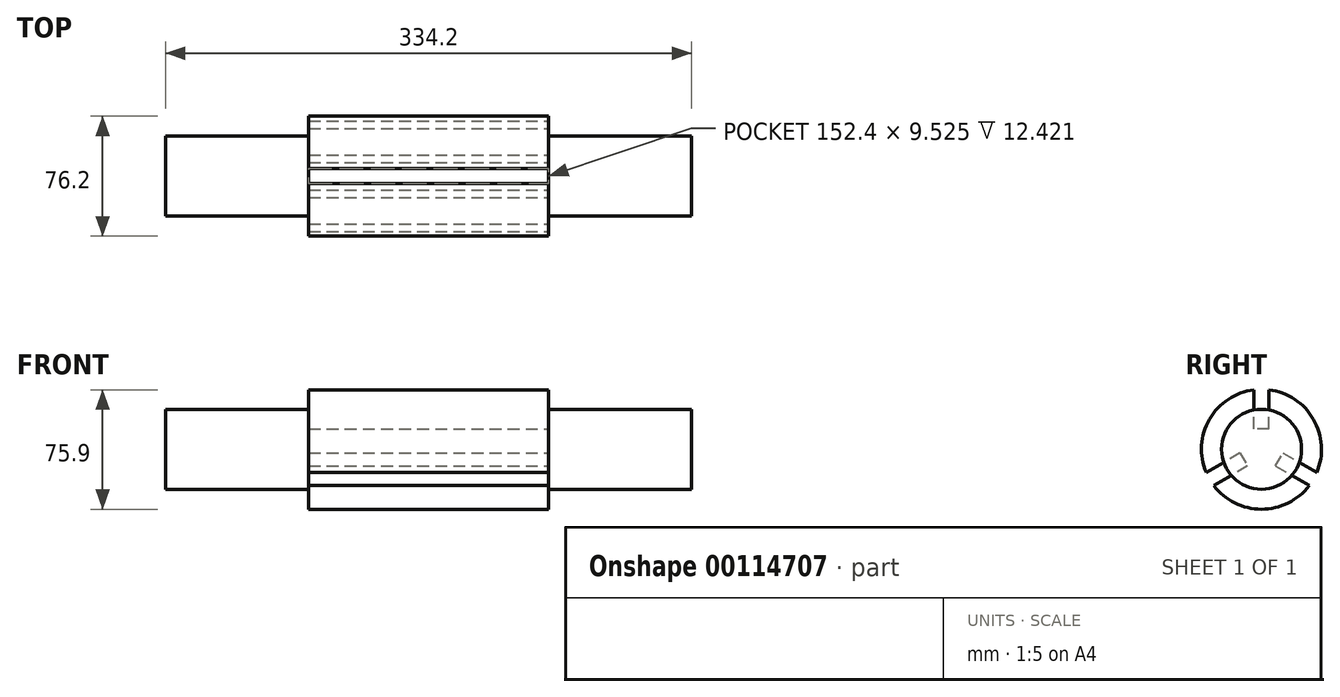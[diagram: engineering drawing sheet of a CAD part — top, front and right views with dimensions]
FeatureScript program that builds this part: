
annotation { "Feature Type Name" : "Feature", "Feature Type Description" : "" }
export const myFeature = defineFeature(function(context is Context, id is Id, definition is map)
    precondition{}
    {
        {
            var Q0;
            Q0=qCreatedBy(makeId("Front.planeOp"),FACE);
            var sketch = newSketch(context, id + "F0", { "sketchPlane" : qUnion([Q0])});
            skLineSegment(sketch, "E0.0", {"start": v(69.85, 0) * mm, "end": v(69.85, 25.4) * mm});
            skLineSegment(sketch, "E1.0", {"start": v(-21.05, 25.4) * mm, "end": v(-21.05, 38.1) * mm});
            skLineSegment(sketch, "E2", {"start": v(69.85, 25.4) * mm, "end": v(-21.05, 25.4) * mm});
            skLineSegment(sketch, "E3.0", {"start": v(-21.05, 38.1) * mm, "end": v(-97.25, 38.1) * mm});
            skLineSegment(sketch, "E4", {"start": v(0, 0) * mm, "end": v(0, 17.35) * mm});
            skLineSegment(sketch, "E5.0", {"start": v(-97.25, 0) * mm, "end": v(-97.25, 38.1) * mm});
            skLineSegment(sketch, "E6.MirrorCS", {"start": v(-173.45, 38.1) * mm, "end": v(-97.25, 38.1) * mm});
            skLineSegment(sketch, "E7.MirrorCS", {"start": v(-173.45, 25.4) * mm, "end": v(-173.45, 38.1) * mm});
            skLineSegment(sketch, "E8.MirrorCS", {"start": v(-264.35, 25.4) * mm, "end": v(-173.45, 25.4) * mm});
            skLineSegment(sketch, "E9.MirrorCS", {"start": v(-264.35, 0) * mm, "end": v(-264.35, 25.4) * mm});
            skLineSegment(sketch, "E10", {"start": v(69.85, 0) * mm, "end": v(-264.35, 0) * mm});
            skSolve(sketch);
        }
        {
            var Q0;
            {var subQ0=sQuery(id+"F0.wireOp",EDGE,"E0.0");Q0=makeQuery(id+"F0.imprint","IMPRINT",FACE,{"disambiguationData":[TD([[makeQuery(id+"F0.imprint","IMPRINT",EDGE,{"derivedFrom":subQ0}),1.0]])]});}
            var Q1;
            {var subQ0=sQuery(id+"F0.wireOp",EDGE,"E5.0");Q1=makeQuery(id+"F0.imprint","IMPRINT",FACE,{"disambiguationData":[TD([[makeQuery(id+"F0.imprint","IMPRINT",EDGE,{"derivedFrom":subQ0}),1.0]])]});}
            var Q2;
            Q2=sQuery(id+"F0.wireOp",EDGE,"E10");
            revolve(context, id + "F1", {"surfaceOperationType" : NewSurfaceOperationType.NEW, "entities" : qUnion([Q0, Q1]), "axis" : qUnion([Q2]), "revolveType" : RevolveType.FULL});
        }
        {
            var Q0;
            Q0=qCreatedBy(makeId("Right.planeOp"),FACE);
            var sketch = newSketch(context, id + "F2", { "sketchPlane" : qUnion([Q0])});
            skCircle(sketch, "E11.0", {"center": v(0, 0) * mm, "radius": 38.1 * mm});
            skCircle(sketch, "E12.0", {"center": v(0, 0) * mm, "radius": 25.4 * mm});
            skLineSegment(sketch, "E13.0", {"start": v(-4.76, 38.1) * mm, "end": v(-4.76, 12.98) * mm});
            skLineSegment(sketch, "E14.0", {"start": v(4.76, 38.1) * mm, "end": v(4.76, 12.98) * mm});
            skLineSegment(sketch, "E15", {"start": v(-4.76, 38.1) * mm, "end": v(4.76, 38.1) * mm});
            skLineSegment(sketch, "E16", {"start": v(-4.76, 12.98) * mm, "end": v(4.76, 12.98) * mm});
            skSolve(sketch);
        }
        {
            var Q0;
            Q0=makeQuery(id+"F1.opRevolve","SWEPT_FACE",FACE,{"disambiguationData":[OSD([sQuery(id+"F0.wireOp",EDGE,"E1.0")])]});
            var sketch = newSketch(context, id + "F3", { "sketchPlane" : qUnion([Q0])});
            skPoint(sketch, "E17.0", {"position": v(0, 12.98) * mm});
            skLineSegment(sketch, "E18.0", {"start": v(-4.76, 38.1) * mm, "end": v(-4.76, 12.98) * mm});
            skLineSegment(sketch, "E19", {"start": v(-4.76, 38.1) * mm, "end": v(4.76, 38.1) * mm});
            skLineSegment(sketch, "E20", {"start": v(4.76, 38.1) * mm, "end": v(4.76, 12.98) * mm});
            skLineSegment(sketch, "E21", {"start": v(-4.76, 12.98) * mm, "end": v(4.76, 12.98) * mm});
            skLineSegment(sketch, "E22.1.0", {"start": v(-8.86, -10.61) * mm, "end": v(-13.62, -2.37) * mm});
            skLineSegment(sketch, "E22.1.1", {"start": v(-30.61, -23.17) * mm, "end": v(-35.38, -14.93) * mm});
            skLineSegment(sketch, "E22.1.2", {"start": v(-30.61, -23.17) * mm, "end": v(-8.86, -10.61) * mm});
            skLineSegment(sketch, "E22.1.3", {"start": v(-35.38, -14.93) * mm, "end": v(-13.62, -2.37) * mm});
            skLineSegment(sketch, "E22.2.0", {"start": v(13.62, -2.37) * mm, "end": v(8.86, -10.61) * mm});
            skLineSegment(sketch, "E22.2.1", {"start": v(35.38, -14.93) * mm, "end": v(30.61, -23.17) * mm});
            skLineSegment(sketch, "E22.2.2", {"start": v(35.38, -14.93) * mm, "end": v(13.62, -2.37) * mm});
            skLineSegment(sketch, "E22.2.3", {"start": v(30.61, -23.17) * mm, "end": v(8.86, -10.61) * mm});
            skPoint(sketch, "E22.center", {"position": v(0, 0) * mm});
            skSolve(sketch);
        }
        {
            var Q0;
            Q0 = qSketchRegion(id + "F3", true);
            var Q1;
            Q1=makeQuery(id+"F1.opRevolve","SWEPT_FACE",FACE,{"disambiguationData":[OSD([sQuery(id+"F0.wireOp",EDGE,"E7.MirrorCS")])]});
            extrude(context, id + "F4", {"entities" : qUnion([Q0]), "operationType" : NewBodyOperationType.REMOVE, "endBound" : BoundingType.UP_TO_SURFACE, "oppositeDirection" : true, "depth" : 25.4 * mm, "endBoundEntityFace" : qUnion([Q1]), "offsetDistance" : 25.4 * mm});
        }
    });
